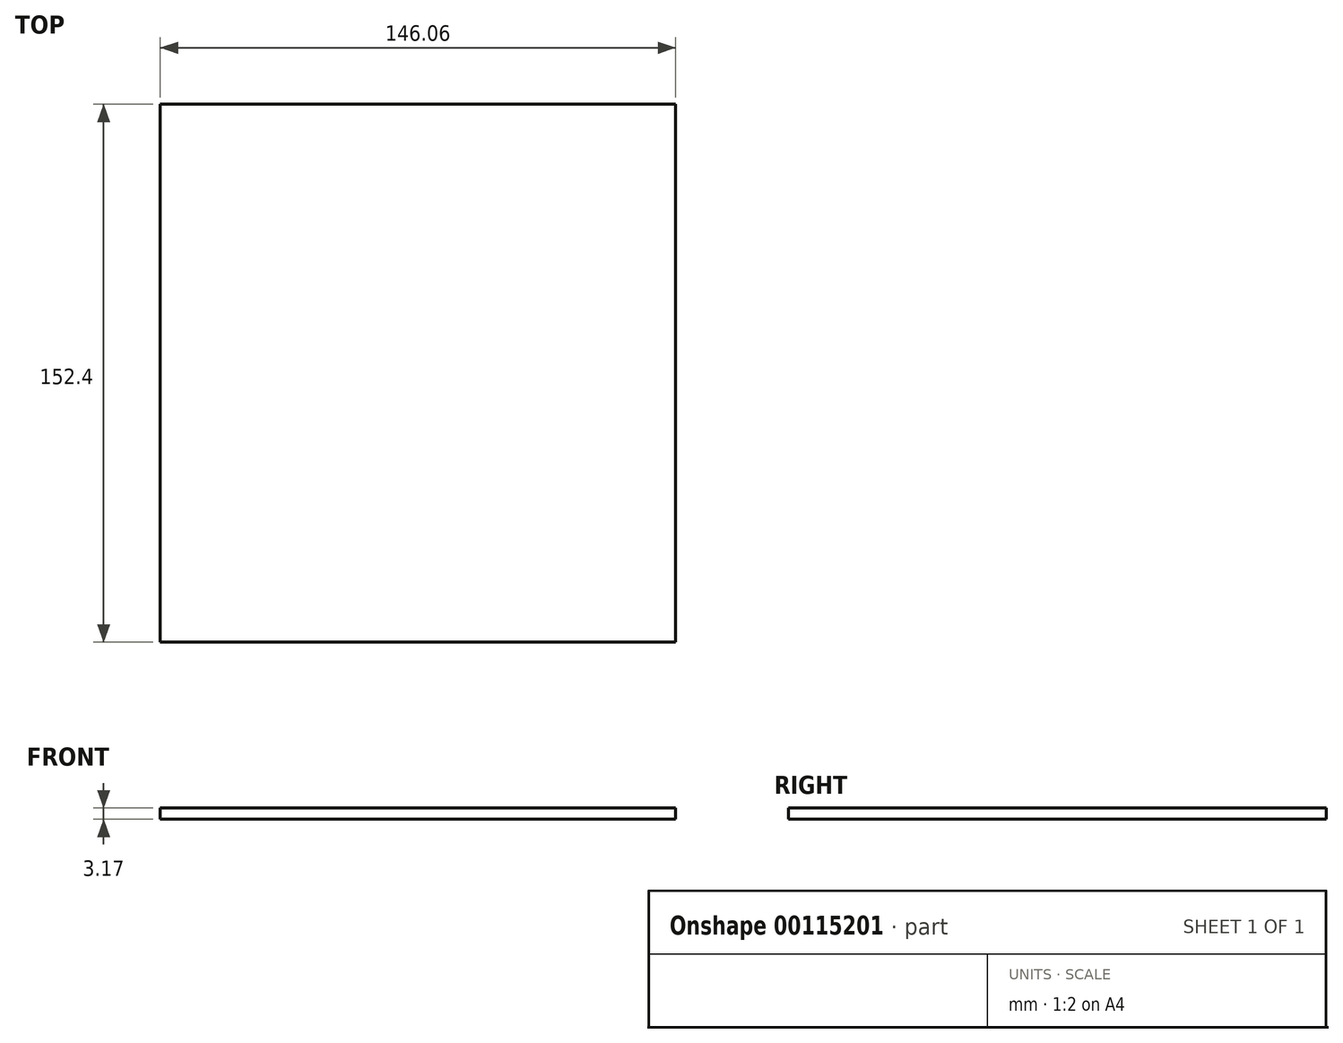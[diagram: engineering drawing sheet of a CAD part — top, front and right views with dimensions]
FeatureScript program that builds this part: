
annotation { "Feature Type Name" : "Feature", "Feature Type Description" : "" }
export const myFeature = defineFeature(function(context is Context, id is Id, definition is map)
    precondition{}
    {
        {
            var Q0;
            Q0=qCreatedBy(makeId("Top.planeOp"),FACE);
            var sketch = newSketch(context, id + "F0", { "sketchPlane" : qUnion([Q0])});
            skLineSegment(sketch, "E0.bottom", {"start": v(-73.02, -76.2) * mm, "end": v(73.03, -76.2) * mm});
            skLineSegment(sketch, "E0.top", {"start": v(-73.03, 76.2) * mm, "end": v(73.02, 76.2) * mm});
            skLineSegment(sketch, "E0.left", {"start": v(-73.02, -76.2) * mm, "end": v(-73.03, 76.2) * mm});
            skLineSegment(sketch, "E0.right", {"start": v(73.03, -76.2) * mm, "end": v(73.02, 76.2) * mm});
            skPoint(sketch, "E0.middle", {"position": v(0, 0) * mm});
            skSolve(sketch);
        }
        {
            var Q0;
            Q0=makeQuery(id+"F0.imprint","IMPRINT",FACE,{"disambiguationData":[TD([[makeQuery(id+"F0.imprint","IMPRINT",EDGE,{"derivedFrom":sQuery(id+"F0.wireOp",EDGE,"E0.bottom")}),1.0]])]});
            extrude(context, id + "F1", {"entities" : qUnion([Q0]), "depth" : 3.17 * mm});
        }
    });
